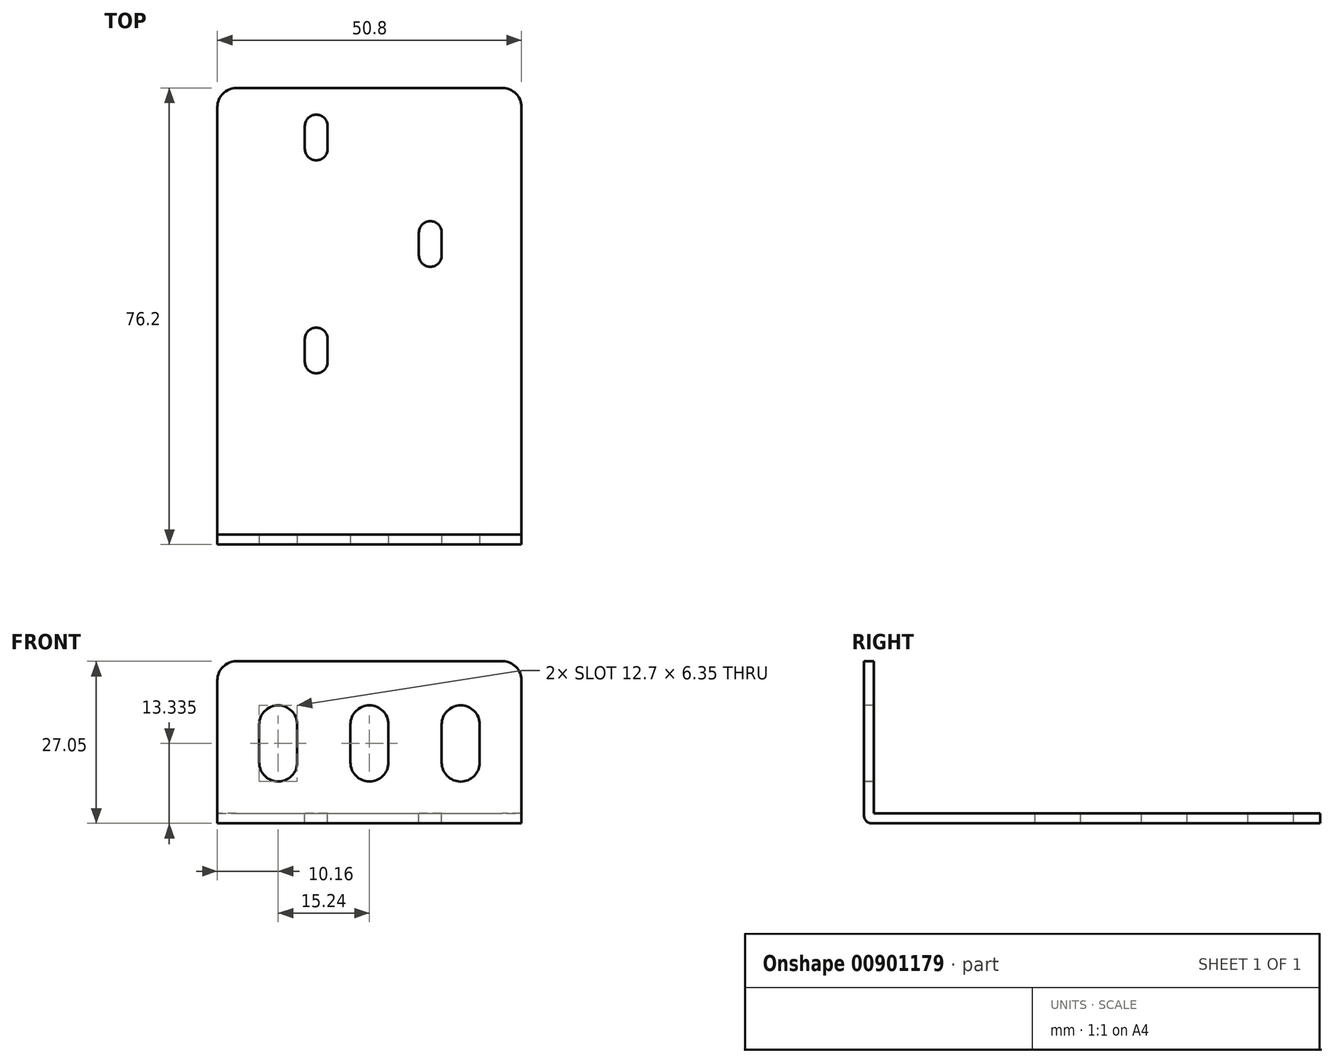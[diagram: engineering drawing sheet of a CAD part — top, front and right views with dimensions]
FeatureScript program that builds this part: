
annotation { "Feature Type Name" : "Feature", "Feature Type Description" : "" }
export const myFeature = defineFeature(function(context is Context, id is Id, definition is map)
    precondition{}
    {
        {
            var Q0;
            Q0=qCreatedBy(makeId("Top.planeOp"),FACE);
            var sketch = newSketch(context, id + "F0", { "sketchPlane" : qUnion([Q0])});
            skLineSegment(sketch, "E0.bottom", {"start": v(-25.4, 34.3) * mm, "end": v(25.4, 34.3) * mm});
            skLineSegment(sketch, "E0.top", {"start": v(-25.4, -41.91) * mm, "end": v(25.4, -41.9) * mm});
            skLineSegment(sketch, "E0.left", {"start": v(-25.4, 34.3) * mm, "end": v(-25.4, -41.91) * mm});
            skLineSegment(sketch, "E0.right", {"start": v(25.4, 34.3) * mm, "end": v(25.4, -41.9) * mm});
            skSolve(sketch);
        }
        {
            var Q0;
            Q0=makeQuery(id+"F0.imprint","IMPRINT",FACE,{"disambiguationData":[TD([[makeQuery(id+"F0.imprint","IMPRINT",EDGE,{"derivedFrom":sQuery(id+"F0.wireOp",EDGE,"E0.bottom")}),-1.0]])]});
            extrude(context, id + "F1", {"entities" : qUnion([Q0]), "depth" : 1.65 * mm, "offsetDistance" : 25.4 * mm});
        }
        {
            var Q0;
            Q0=makeQuery(id+"F1.opExtrude","CAP_FACE",FACE,{"disambiguationData":[OSD([sQuery(id+"F0.wireOp",EDGE,"E0.bottom"),sQuery(id+"F0.wireOp",EDGE,"E0.top"),sQuery(id+"F0.wireOp",EDGE,"E0.left"),sQuery(id+"F0.wireOp",EDGE,"E0.right")])],"isStart":false});
            var sketch = newSketch(context, id + "F2", { "sketchPlane" : qUnion([Q0])});
            skLineSegment(sketch, "E1.bottom", {"start": v(-25.4, -41.91) * mm, "end": v(25.4, -41.91) * mm});
            skLineSegment(sketch, "E1.top", {"start": v(-25.4, -40.26) * mm, "end": v(25.4, -40.26) * mm});
            skLineSegment(sketch, "E1.left", {"start": v(-25.4, -41.91) * mm, "end": v(-25.4, -40.26) * mm});
            skLineSegment(sketch, "E1.right", {"start": v(25.4, -41.91) * mm, "end": v(25.4, -40.26) * mm});
            skSolve(sketch);
        }
        {
            var Q0;
            Q0=makeQuery(id+"F2.imprint","IMPRINT",FACE,{"disambiguationData":[TD([[makeQuery(id+"F2.imprint","IMPRINT",EDGE,{"derivedFrom":sQuery(id+"F2.wireOp",EDGE,"E1.bottom")}),1.0]])]});
            extrude(context, id + "F3", {"entities" : qUnion([Q0]), "operationType" : NewBodyOperationType.ADD, "depth" : 25.4 * mm, "offsetDistance" : 25.4 * mm});
        }
        {
            var Q0;
            Q0=makeQuery(id+"F1.opExtrude","CAP_EDGE",EDGE,{"disambiguationData":[OSD([sQuery(id+"F0.wireOp",EDGE,"E0.top")])],"isStart":true});
            fillet(context, id + "F4", {"entities" : qUnion([Q0]), "radius" : 1.27 * mm, "tangentPropagation" : true, "allowEdgeOverflow" : false});
        }
        {
            var Q0;
            Q0=makeQuery(id+"F1.opExtrude","SWEPT_EDGE",EDGE,{"disambiguationData":[OSD([sQuery(id+"F0.wireOp",EDGE,"E0.bottom"),sQuery(id+"F0.wireOp",EDGE,"E0.right")])]});
            var Q1;
            Q1=makeQuery(id+"F1.opExtrude","SWEPT_EDGE",EDGE,{"disambiguationData":[OSD([sQuery(id+"F0.wireOp",EDGE,"E0.bottom"),sQuery(id+"F0.wireOp",EDGE,"E0.left")])]});
            var Q2;
            Q2=makeQuery(id+"F3.opExtrude","CAP_EDGE",EDGE,{"disambiguationData":[OSD([sQuery(id+"F2.wireOp",EDGE,"E1.right")])],"isStart":false});
            var Q3;
            Q3=makeQuery(id+"F3.opExtrude","CAP_EDGE",EDGE,{"disambiguationData":[OSD([sQuery(id+"F2.wireOp",EDGE,"E1.left")])],"isStart":false});
            fillet(context, id + "F5", {"entities" : qUnion([Q0, Q1, Q2, Q3]), "radius" : 3.17 * mm, "tangentPropagation" : true, "allowEdgeOverflow" : false});
        }
        {
            var Q0;
            Q0=makeQuery(id+"F1.opExtrude","CAP_FACE",FACE,{"disambiguationData":[OSD([sQuery(id+"F0.wireOp",EDGE,"E0.bottom"),sQuery(id+"F0.wireOp",EDGE,"E0.top"),sQuery(id+"F0.wireOp",EDGE,"E0.left"),sQuery(id+"F0.wireOp",EDGE,"E0.right")])],"isStart":false});
            var sketch = newSketch(context, id + "F6", { "sketchPlane" : qUnion([Q0])});
            skPoint(sketch, "E2", {"position": v(10.16, 6.35) * mm});
            skPoint(sketch, "E3", {"position": v(10.16, 10.16) * mm});
            skArc(sketch, "E4", {"start": v(12.07, 10.16) * mm, "mid": v(10.16, 12.07) * mm, "end": v(8.26, 10.16) * mm});
            skArc(sketch, "E5", {"start": v(8.26, 6.35) * mm, "mid": v(10.16, 4.45) * mm, "end": v(12.07, 6.35) * mm});
            skLineSegment(sketch, "E6.bottom", {"start": v(8.26, 10.16) * mm, "end": v(10.16, 10.16) * mm});
            skLineSegment(sketch, "E6.top", {"start": v(8.26, 6.35) * mm, "end": v(10.16, 6.35) * mm});
            skLineSegment(sketch, "E6.left", {"start": v(8.26, 10.16) * mm, "end": v(8.26, 6.35) * mm});
            skLineSegment(sketch, "E6.right", {"start": v(12.07, 10.16) * mm, "end": v(12.07, 6.35) * mm});
            skArc(sketch, "E7", {"start": v(-6.98, 27.94) * mm, "mid": v(-8.89, 29.85) * mm, "end": v(-10.8, 27.94) * mm});
            skArc(sketch, "E8", {"start": v(-10.8, 24.13) * mm, "mid": v(-8.89, 22.23) * mm, "end": v(-6.98, 24.13) * mm});
            skLineSegment(sketch, "E9.left", {"start": v(-10.8, 27.94) * mm, "end": v(-10.8, 24.13) * mm});
            skLineSegment(sketch, "E9.right", {"start": v(-6.98, 27.94) * mm, "end": v(-6.98, 24.13) * mm});
            skArc(sketch, "E10", {"start": v(-6.98, -7.62) * mm, "mid": v(-8.89, -5.71) * mm, "end": v(-10.8, -7.62) * mm});
            skArc(sketch, "E11", {"start": v(-10.8, -11.43) * mm, "mid": v(-8.89, -13.33) * mm, "end": v(-6.98, -11.43) * mm});
            skLineSegment(sketch, "E12.left", {"start": v(-10.8, -7.62) * mm, "end": v(-10.8, -11.43) * mm});
            skLineSegment(sketch, "E12.right", {"start": v(-6.98, -7.62) * mm, "end": v(-6.98, -11.43) * mm});
            skSolve(sketch);
        }
        {
            var Q0;
            Q0=makeQuery(id+"F6.imprint","IMPRINT",FACE,{"disambiguationData":[TD([[makeQuery(id+"F6.imprint","IMPRINT",EDGE,{"derivedFrom":sQuery(id+"F6.wireOp",EDGE,"E7")}),1.0]])]});
            var Q1;
            Q1=makeQuery(id+"F6.imprint","IMPRINT",FACE,{"disambiguationData":[TD([[makeQuery(id+"F6.imprint","IMPRINT",EDGE,{"derivedFrom":sQuery(id+"F6.wireOp",EDGE,"E4")}),1.0]])]});
            var Q2;
            Q2=makeQuery(id+"F6.imprint","IMPRINT",FACE,{"disambiguationData":[TD([[makeQuery(id+"F6.imprint","IMPRINT",EDGE,{"derivedFrom":sQuery(id+"F6.wireOp",EDGE,"E10")}),1.0]])]});
            extrude(context, id + "F7", {"entities" : qUnion([Q0, Q1, Q2]), "operationType" : NewBodyOperationType.REMOVE, "oppositeDirection" : true, "depth" : 25.4 * mm, "offsetDistance" : 25.4 * mm});
        }
        {
            var Q0;
            Q0=makeQuery(id+"F3.boolean.opBoolean","MERGE",FACE,{"derivedFrom":[makeQuery(id+"F1.opExtrude","SWEPT_FACE",FACE,{"disambiguationData":[OSD([sQuery(id+"F0.wireOp",EDGE,"E0.top")])]}),makeQuery(id+"F3.opExtrude","SWEPT_FACE",FACE,{"disambiguationData":[OSD([sQuery(id+"F2.wireOp",EDGE,"E1.bottom")])]})]});
            var sketch = newSketch(context, id + "F8", { "sketchPlane" : qUnion([Q0])});
            skPoint(sketch, "E13", {"position": v(-15.24, 16.51) * mm});
            skPoint(sketch, "E14", {"position": v(-15.24, 10.16) * mm});
            skLineSegment(sketch, "E15.left", {"start": v(-18.41, 16.51) * mm, "end": v(-18.41, 10.16) * mm});
            skLineSegment(sketch, "E15.right", {"start": v(-12.06, 16.51) * mm, "end": v(-12.06, 10.16) * mm});
            skArc(sketch, "E16", {"start": v(-12.06, 16.51) * mm, "mid": v(-15.24, 19.69) * mm, "end": v(-18.41, 16.51) * mm});
            skArc(sketch, "E17", {"start": v(-18.41, 10.16) * mm, "mid": v(-15.24, 6.99) * mm, "end": v(-12.06, 10.16) * mm});
            skPoint(sketch, "E18", {"position": v(0, 10.16) * mm});
            skPoint(sketch, "E19", {"position": v(0, 16.51) * mm});
            skPoint(sketch, "E20", {"position": v(15.24, 16.51) * mm});
            skLineSegment(sketch, "E21.bottom", {"start": v(0, 16.51) * mm, "end": v(3.18, 16.51) * mm});
            skLineSegment(sketch, "E21.top", {"start": v(0, 10.16) * mm, "end": v(3.18, 10.16) * mm});
            skLineSegment(sketch, "E21.right", {"start": v(3.18, 16.51) * mm, "end": v(3.18, 10.16) * mm});
            skLineSegment(sketch, "E22.bottom", {"start": v(15.24, 16.51) * mm, "end": v(18.41, 16.51) * mm});
            skLineSegment(sketch, "E22.right", {"start": v(18.41, 16.51) * mm, "end": v(18.41, 12.81) * mm});
            skArc(sketch, "E23", {"start": v(3.18, 16.51) * mm, "mid": v(0, 19.69) * mm, "end": v(-3.18, 16.51) * mm});
            skArc(sketch, "E24", {"start": v(-3.18, 10.16) * mm, "mid": v(0, 6.99) * mm, "end": v(3.18, 10.16) * mm});
            skArc(sketch, "E25", {"start": v(18.41, 16.51) * mm, "mid": v(15.24, 19.69) * mm, "end": v(12.06, 16.51) * mm});
            skLineSegment(sketch, "E26.right", {"start": v(-3.18, 16.51) * mm, "end": v(-3.18, 10.16) * mm});
            skLineSegment(sketch, "E27.bottom", {"start": v(18.41, 16.51) * mm, "end": v(15.24, 16.51) * mm});
            skLineSegment(sketch, "E27.top", {"start": v(18.41, 10.14) * mm, "end": v(15.24, 10.14) * mm});
            skLineSegment(sketch, "E27.left", {"start": v(18.41, 16.51) * mm, "end": v(18.41, 10.14) * mm});
            skLineSegment(sketch, "E27.right", {"start": v(12.06, 16.51) * mm, "end": v(12.06, 10.14) * mm});
            skArc(sketch, "E28", {"start": v(12.06, 10.14) * mm, "mid": v(15.24, 6.96) * mm, "end": v(18.41, 10.14) * mm});
            skSolve(sketch);
        }
        {
            var Q0;
            Q0=makeQuery(id+"F8.imprint","IMPRINT",FACE,{"disambiguationData":[TD([[makeQuery(id+"F8.imprint","IMPRINT",EDGE,{"derivedFrom":sQuery(id+"F8.wireOp",EDGE,"E15.left")}),1.0]])]});
            var Q1;
            Q1=makeQuery(id+"F8.imprint","IMPRINT",FACE,{"disambiguationData":[TD([[makeQuery(id+"F8.imprint","IMPRINT",EDGE,{"derivedFrom":sQuery(id+"F8.wireOp",EDGE,"E23")}),1.0]])]});
            var Q2;
            Q2=makeQuery(id+"F8.imprint","IMPRINT",FACE,{"disambiguationData":[TD([[makeQuery(id+"F8.imprint","IMPRINT",EDGE,{"derivedFrom":sQuery(id+"F8.wireOp",EDGE,"E25")}),1.0]])]});
            extrude(context, id + "F9", {"entities" : qUnion([Q0, Q1, Q2]), "operationType" : NewBodyOperationType.REMOVE, "oppositeDirection" : true, "depth" : 25.4 * mm, "offsetDistance" : 25.4 * mm});
        }
    });
